SOLIDWORKS PART (.sldprt)
format: sldprt  version: not decoded by parser v0  size: 162,816 bytes
history: native  units: mm
features: sketch x7, plane x4, helix x3, material x1, sweep x1 (+10 scaffold rows collapsed)
feature tree (26):
  scaffold x10  (default folders/planes/origin — collapsed)
  material  "Matériau <non spécifié>"
  plane  "Plan de face"
  plane  "Plan de dessus"
  plane  "Plan de droite"
  sketch  "Esquisse1"  dims[D1=~3.221968mm]
  sketch  "Esquisse2"  dims[D1=~0.126525mm]
  sweep  "Balayage1"
  plane  "Plan1"  Offset=1mm
  sketch  "Esquisse3"  dims[D1=~2.083559mm]
  sketch  "Esquisse5"
  helix  "Hélice/Spirale1"  Pitch=1mm
  sketch  "Esquisse6"  dims[D1=~0.508276mm]
  helix  "Balayage2"  [1 undecoded]
  sketch  "Esquisse7"  dims[D1=1.5mm]
  sketch  "Esquisse8"  dims[D1=0.5mm]
  helix  "Balayage5"  [1 undecoded]
decode coverage: 7 of 11 modeling features carry decoded parameters
note: ~ marks probable driven/reference dimensions
note: 2 parameter values undecoded
note: suppression state not decoded; provenance and decode notes live in map.json
